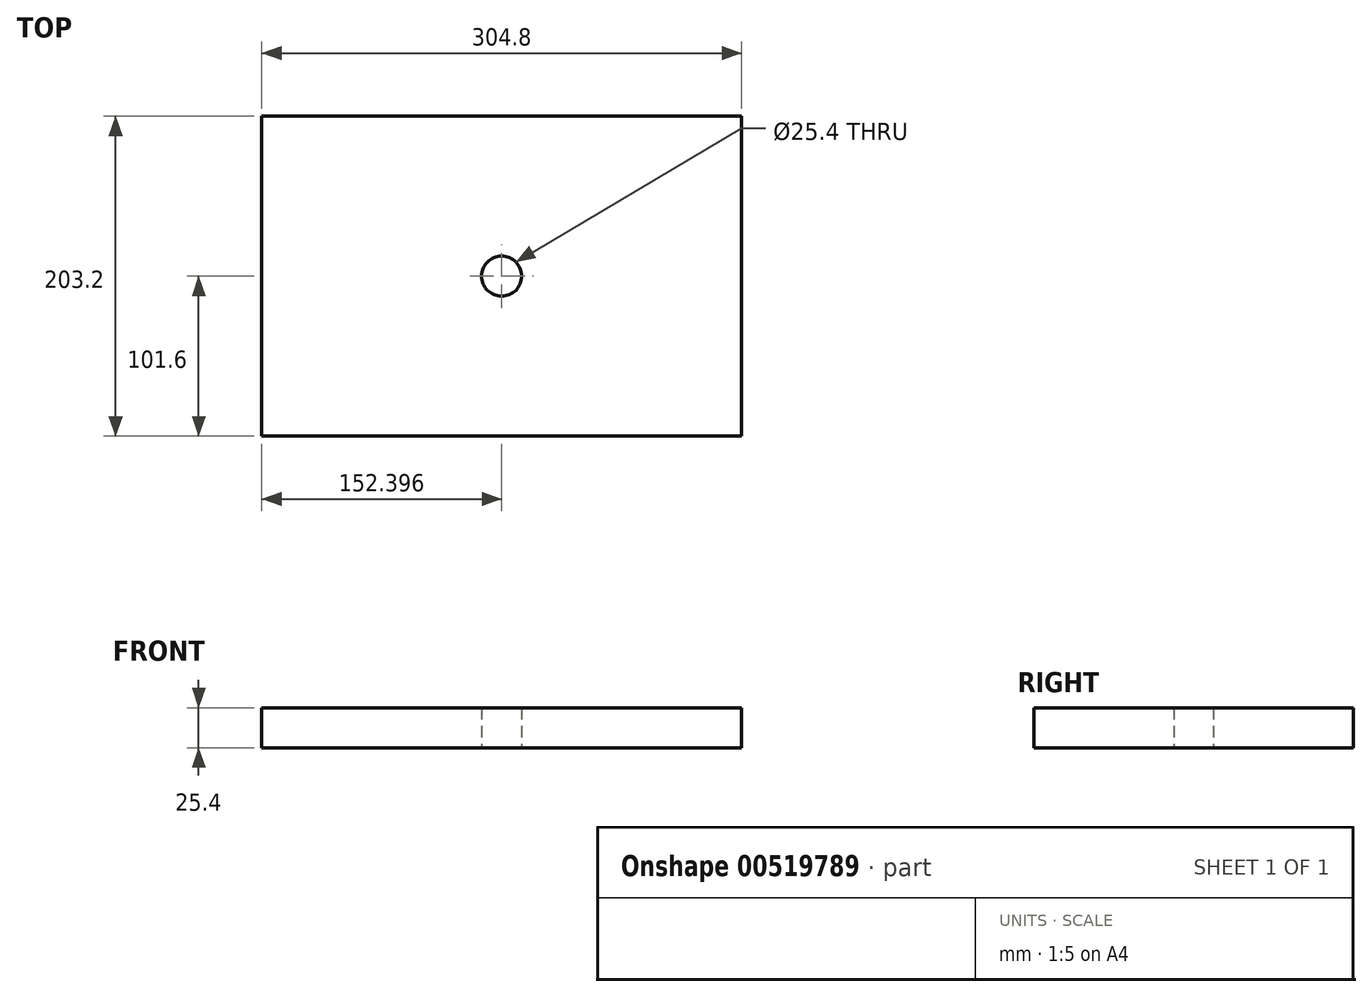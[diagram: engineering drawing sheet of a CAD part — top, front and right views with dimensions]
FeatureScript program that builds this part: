
annotation { "Feature Type Name" : "Feature", "Feature Type Description" : "" }
export const myFeature = defineFeature(function(context is Context, id is Id, definition is map)
    precondition{}
    {
        {
            var Q0;
            Q0=qCreatedBy(makeId("Top.planeOp"),FACE);
            var sketch = newSketch(context, id + "F0", { "sketchPlane" : qUnion([Q0])});
            skLineSegment(sketch, "E0.bottom", {"start": v(-50.23, 203.2) * mm, "end": v(254.57, 203.2) * mm});
            skLineSegment(sketch, "E0.top", {"start": v(-50.23, 0) * mm, "end": v(254.57, 0) * mm});
            skLineSegment(sketch, "E0.left", {"start": v(-50.23, 203.2) * mm, "end": v(-50.23, 0) * mm});
            skLineSegment(sketch, "E0.right", {"start": v(254.57, 203.2) * mm, "end": v(254.57, 0) * mm});
            skCircle(sketch, "E1", {"center": v(102.17, 101.6) * mm, "radius": 12.7 * mm});
            skPoint(sketch, "E1.centerSnap0", {"position": v(-50.23, 101.6) * mm});
            skPoint(sketch, "E1.centerSnap1", {"position": v(102.17, 203.2) * mm});
            skSolve(sketch);
        }
        {
            var Q0;
            Q0=makeQuery(id+"F0.imprint","IMPRINT",FACE,{"disambiguationData":[TD([[makeQuery(id+"F0.imprint","IMPRINT",EDGE,{"derivedFrom":sQuery(id+"F0.wireOp",EDGE,"E0.bottom")}),-1.0]])]});
            extrude(context, id + "F1", {"entities" : qUnion([Q0]), "depth" : 25.4 * mm, "offsetDistance" : 25.4 * mm});
        }
    });
